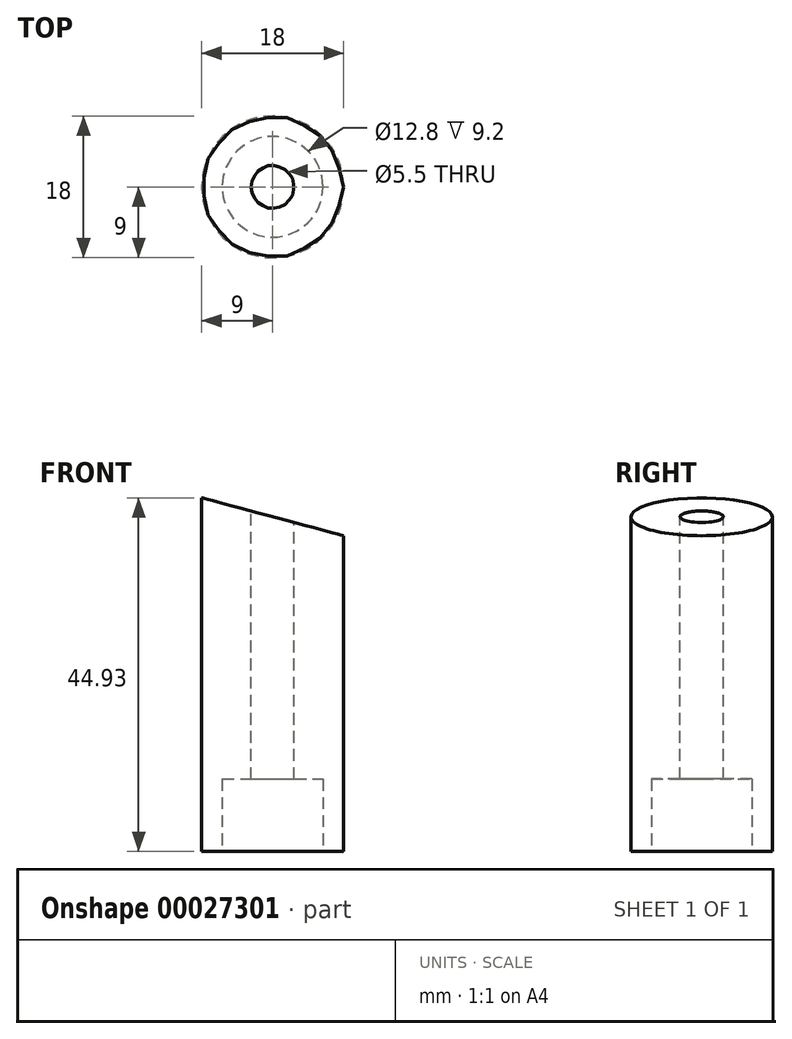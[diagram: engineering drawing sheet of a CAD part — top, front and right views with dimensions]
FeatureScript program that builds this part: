
annotation { "Feature Type Name" : "Feature", "Feature Type Description" : "" }
export const myFeature = defineFeature(function(context is Context, id is Id, definition is map)
    precondition{}
    {
        {
            var Q0;
            Q0=qCreatedBy(makeId("Top.planeOp"),FACE);
            var sketch = newSketch(context, id + "F0", { "sketchPlane" : qUnion([Q0])});
            skCircle(sketch, "E0", {"center": v(0, 0) * mm, "radius": 9 * mm});
            skSolve(sketch);
        }
        {
            var Q0;
            Q0=qSketchRegion(id+"F0",true);
            extrude(context, id + "F1", {"entities" : qUnion([Q0]), "depth" : 45 * mm, "offsetDistance" : 25 * mm});
        }
        {
            var Q0;
            Q0=makeQuery(id+"F1.opExtrude","CAP_FACE",FACE,{"disambiguationData":[OSD([sQuery(id+"F0.wireOp",EDGE,"E0")])],"isStart":true});
            var sketch = newSketch(context, id + "F2", { "sketchPlane" : qUnion([Q0])});
            skCircle(sketch, "E1", {"center": v(0, 0) * mm, "radius": 6.4 * mm});
            skSolve(sketch);
        }
        {
            var Q0;
            Q0=qSketchRegion(id+"F2",true);
            extrude(context, id + "F3", {"entities" : qUnion([Q0]), "operationType" : NewBodyOperationType.REMOVE, "oppositeDirection" : true, "depth" : 9.2 * mm, "offsetDistance" : 25 * mm});
        }
        {
            var Q0;
            Q0=makeQuery(id+"F1.opExtrude","CAP_FACE",FACE,{"disambiguationData":[OSD([sQuery(id+"F0.wireOp",EDGE,"E0")])],"isStart":false});
            var sketch = newSketch(context, id + "F4", { "sketchPlane" : qUnion([Q0])});
            skCircle(sketch, "E2", {"center": v(0, 0) * mm, "radius": 2.75 * mm});
            skSolve(sketch);
        }
        {
            var Q0;
            Q0=qSketchRegion(id+"F4",true);
            extrude(context, id + "F5", {"entities" : qUnion([Q0]), "operationType" : NewBodyOperationType.REMOVE, "endBound" : BoundingType.THROUGH_ALL, "oppositeDirection" : true, "depth" : 25 * mm, "offsetDistance" : 25 * mm});
        }
        {
            var Q0;
            Q0=qCreatedBy(makeId("Front.planeOp"),FACE);
            var sketch = newSketch(context, id + "F6", { "sketchPlane" : qUnion([Q0])});
            skLineSegment(sketch, "E3", {"start": v(-17.7, 47.26) * mm, "end": v(12.5, 47.26) * mm});
            skLineSegment(sketch, "E4", {"start": v(-17.7, 47.26) * mm, "end": v(14.51, 38.63) * mm});
            skLineSegment(sketch, "E5", {"start": v(12.5, 47.26) * mm, "end": v(14.51, 38.63) * mm});
            skSolve(sketch);
        }
        {
            var Q0;
            Q0=qSketchRegion(id+"F6",true);
            extrude(context, id + "F7", {"entities" : qUnion([Q0]), "operationType" : NewBodyOperationType.REMOVE, "endBound" : BoundingType.SYMMETRIC, "oppositeDirection" : true, "depth" : 25 * mm, "offsetDistance" : 25 * mm});
        }
    });
